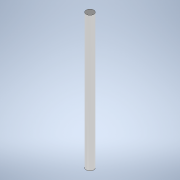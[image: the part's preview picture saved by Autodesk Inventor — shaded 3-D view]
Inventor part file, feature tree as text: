
AUTODESK INVENTOR PART (.ipt)
format: ipt  version: 2022 (Build 260153000, 153)  size: 91,648 bytes
history: native  units: mm
features: extrude x1, sketch x1
ambient origin geometry x8: Origin, YZ Plane, XZ Plane, XY Plane, X Axis, Y Axis, Z Axis, Center Point
bodies: Solid1 (feature_tree)
feature tree (2):
  extrude  "Extrusion1"  Depth=35.5mm TaperAngle=0.0deg
  sketch  "Sketch1"  dims[d0=2.0mm d1=35.5mm d2=0.0mm]
